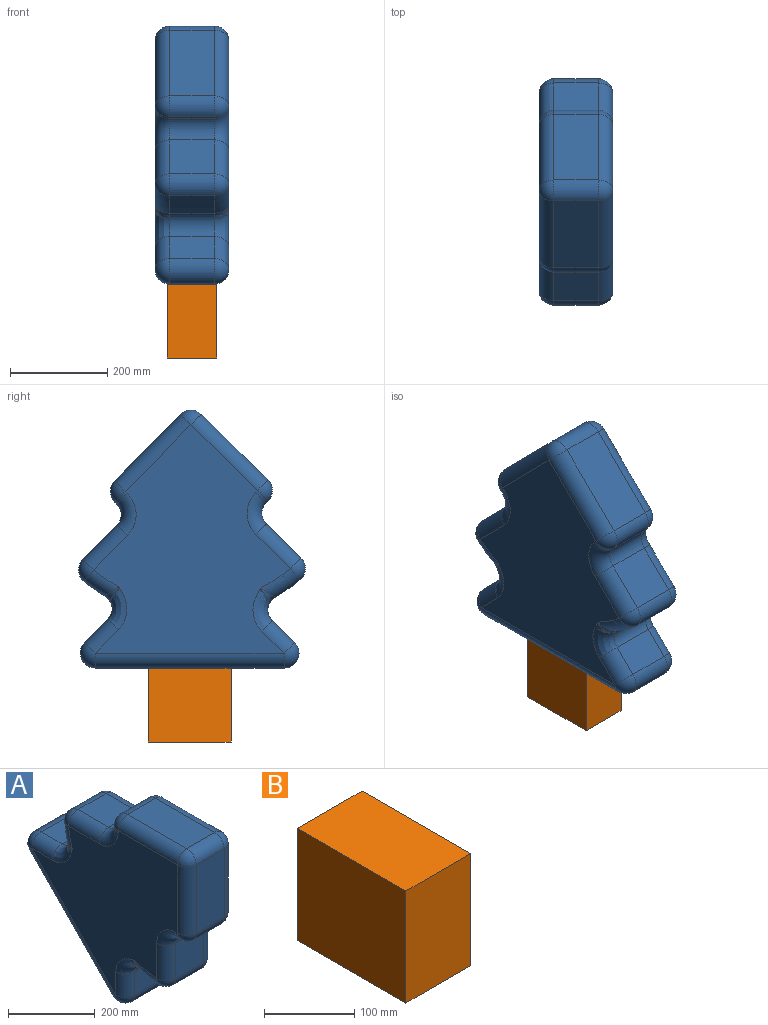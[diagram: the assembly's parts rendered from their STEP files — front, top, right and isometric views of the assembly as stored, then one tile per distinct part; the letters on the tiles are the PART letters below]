
ASSEMBLY  parts=2 mates=1
PART A: 72 faces, bbox 213.7x534.7x528.2 mm
  f0: cylinder r=349.59mm len=91.08mm, axis (-1,0,0), area 4696.8mm2, adj f2,f19,f20,f70
  f1: torus R=318.93mm, axis (1,0,0), area 3328.4mm2, adj f7,f11,f25,f53
  f2: torus R=318.93mm, axis (1,0,0), area 2790.6mm2, adj f0,f5,f26,f68
  f3: plane 99.76x91.08mm, normal (0,-1,0), area 9086.2mm2, adj f29,f30,f40,f41
  f4: plane 99.76x91.08mm, normal (0,0,1), area 9086.2mm2, adj f13,f14,f20,f21
  f5: plane 473.42x466.9mm, normal (-1,0,0), area 117312.5mm2, adj f2,f17,f21,f22,f31,f32,f41,f42
  f6: plane 192.68x91.08mm, normal (0,-1,0), area 17549mm2, adj f33,f34,f42,f43
  f7: plane 473.42x466.91mm, normal (1,0,0), area 117312.5mm2, adj f1,f12,f13,f15,f19,f24,f29,f34
  f8: plane 91.08x5.65mm, normal (0,1,0), area 514.6mm2, adj f14,f15,f22,f23
  f9: plane 192.68x91.08mm, normal (0,0,1), area 17549mm2, adj f23,f24,f32,f33
  f10: plane 91.08x5.65mm, normal (0,0,-1), area 514.6mm2, adj f35,f40,f43,f46
  f11: cylinder r=349.59mm len=91.08mm, axis (-1,0,0), area 5649mm2, adj f1,f30,f31,f51
  f12: torus R=61.32mm, axis (1,0,0), area 3162.4mm2, adj f7,f13,f14,f15
  f13: cylinder r=30.66mm len=99.76mm, axis (0,-1,0), area 4804.7mm2, adj f4,f7,f12,f16
  f14: cylinder r=30.66mm len=91.08mm, axis (1,0,0), area 4386.5mm2, adj f4,f8,f12,f17
  f15: cylinder r=30.66mm len=30.66mm, axis (0,0,-1), area 272.1mm2, adj f7,f8,f12,f18
  f16: sphere r=30.66mm, area 952.7mm2, adj f13,f19,f20
  f17: torus R=61.32mm, axis (1,0,0), area 3162.4mm2, adj f5,f14,f21,f22
  f18: sphere r=30.66mm, area 940.1mm2, adj f15,f23,f24
  f19: torus R=318.93mm, axis (1,0,0), area 2790.6mm2, adj f0,f7,f16,f71
  f20: cylinder r=30.66mm len=91.08mm, axis (-1,0,0), area 4655.4mm2, adj f0,f4,f16,f26
  f21: cylinder r=30.66mm len=99.76mm, axis (0,1,0), area 4804.7mm2, adj f4,f5,f17,f26
  f22: cylinder r=30.66mm len=30.66mm, axis (0,0,1), area 272.1mm2, adj f5,f8,f17,f27
  f23: cylinder r=30.66mm len=91.08mm, axis (1,0,0), area 4386.5mm2, adj f8,f9,f18,f27
  f24: cylinder r=30.66mm len=192.68mm, axis (0,-1,0), area 9279.7mm2, adj f7,f9,f18,f28
  f25: sphere r=30.66mm, area 1567.2mm2, adj f1,f29,f30
  f26: sphere r=30.66mm, area 2142.7mm2, adj f2,f20,f21
  f27: sphere r=30.66mm, area 2013.2mm2, adj f22,f23,f32
  f28: sphere r=30.66mm, area 1476.7mm2, adj f24,f33,f34
  f29: cylinder r=30.66mm len=99.76mm, axis (0,0,1), area 4804.7mm2, adj f3,f7,f25,f36
  f30: cylinder r=30.66mm len=91.08mm, axis (-1,0,0), area 4655.4mm2, adj f3,f11,f25,f37
  f31: torus R=318.93mm, axis (1,0,0), area 3328.4mm2, adj f5,f11,f37,f50
  f32: cylinder r=30.66mm len=192.68mm, axis (0,1,0), area 9279.7mm2, adj f5,f9,f27,f38
  f33: cylinder r=30.66mm len=91.08mm, axis (1,0,0), area 4386.5mm2, adj f6,f9,f28,f38
  f34: cylinder r=30.66mm len=192.68mm, axis (0,0,1), area 9279.7mm2, adj f6,f7,f28,f39
  f35: cylinder r=30.66mm len=30.66mm, axis (0,1,0), area 272.1mm2, adj f7,f10,f36,f39
  f36: torus R=61.32mm, axis (1,0,0), area 3162.4mm2, adj f7,f29,f35,f40
  f37: sphere r=30.66mm, area 1567.2mm2, adj f30,f31,f41
  f38: sphere r=30.66mm, area 1476.7mm2, adj f32,f33,f42
  f39: sphere r=30.66mm, area 1476.7mm2, adj f34,f35,f43
  f40: cylinder r=30.66mm len=91.08mm, axis (1,0,0), area 4386.5mm2, adj f3,f10,f36,f44
  f41: cylinder r=30.66mm len=99.76mm, axis (0,0,-1), area 4804.7mm2, adj f3,f5,f37,f44
  f42: cylinder r=30.66mm len=192.68mm, axis (0,0,-1), area 9279.7mm2, adj f5,f6,f38,f45
  f43: cylinder r=30.66mm len=91.08mm, axis (1,0,0), area 4386.5mm2, adj f6,f10,f39,f45
  f44: torus R=61.32mm, axis (1,0,0), area 3162.4mm2, adj f5,f40,f41,f46
  f45: sphere r=30.66mm, area 1476.7mm2, adj f42,f43,f46
  f46: cylinder r=30.66mm len=30.66mm, axis (0,-1,0), area 272.1mm2, adj f5,f10,f44,f45
  f47: plane 91.08x68.11mm, normal (0,0,1), area 6203.5mm2, adj f62,f64,f67,f68,f70,f71
  f48: plane 91.08x64.5mm, normal (0,-1,0), area 5874.9mm2, adj f50,f51,f53,f54,f57,f58
  f49: plane 277.49x273.01mm, normal (0,0.71,-0.7), area 35457.2mm2, adj f57,f59,f62,f63
  f50: bspline ~71.09x69.35mm, area 550.9mm2, adj f31,f48,f51,f52
  f51: cylinder r=30.66mm len=91.08mm, axis (-1,0,0), area 5150.4mm2, adj f11,f48,f50,f53
  f52: bspline ~71.08x61.32mm, area 2905.4mm2, adj f5,f50,f54
  f53: bspline ~71.09x69.35mm, area 550.9mm2, adj f1,f48,f51,f55
  f54: cylinder r=30.66mm len=64.5mm, axis (0,0,1), area 3106.1mm2, adj f5,f48,f52,f56
  f55: bspline ~71.08x61.32mm, area 2905.3mm2, adj f7,f53,f58
  f56: sphere r=30.66mm, area 2557.5mm2, adj f54,f57,f59
  f57: cylinder r=30.66mm len=91.08mm, axis (-1,0,0), area 6602.2mm2, adj f48,f49,f56,f60
  f58: cylinder r=30.66mm len=64.5mm, axis (0,0,-1), area 3106.1mm2, adj f7,f48,f55,f60
  f59: cylinder r=30.66mm len=298.99mm, axis (0,-0.7,-0.71), area 18746.5mm2, adj f5,f49,f56,f61
  f60: sphere r=30.66mm, area 2557.5mm2, adj f57,f58,f63
  f61: sphere r=30.66mm, area 2558.3mm2, adj f59,f62,f64
  f62: cylinder r=30.66mm len=91.08mm, axis (1,0,0), area 6556.8mm2, adj f47,f49,f61,f65
  f63: cylinder r=30.66mm len=298.99mm, axis (0,0.7,0.71), area 18746.5mm2, adj f7,f49,f60,f65
  f64: cylinder r=30.66mm len=68.11mm, axis (0,1,0), area 3279.8mm2, adj f5,f47,f61,f66
  f65: sphere r=30.66mm, area 2021.9mm2, adj f62,f63,f67
  f66: bspline ~70.47x61.32mm, area 2933.5mm2, adj f5,f64,f68
  f67: cylinder r=30.66mm len=68.11mm, axis (0,-1,0), area 3279.8mm2, adj f7,f47,f65,f69
  f68: bspline ~69.5x65.39mm, area 487.4mm2, adj f2,f47,f66,f70
  f69: bspline ~70.47x61.32mm, area 2933.5mm2, adj f7,f67,f71
  f70: cylinder r=30.66mm len=91.08mm, axis (-1,0,0), area 5066.9mm2, adj f0,f47,f68,f71
  f71: bspline ~69.5x65.39mm, area 487.4mm2, adj f19,f47,f69,f70
PART B: 6 faces, bbox 101.6x170.5x152.4 mm
  f0: plane 170.46x152.4mm, normal (-1,0,0), area 25978.4mm2, adj f1,f3,f4,f5
  f1: plane 152.4x101.6mm, normal (0,-1,0), area 15483.8mm2, adj f0,f2,f4,f5
  f2: plane 170.46x152.4mm, normal (1,0,0), area 25978.4mm2, adj f1,f3,f4,f5
  f3: plane 152.4x101.6mm, normal (0,1,0), area 15483.8mm2, adj f0,f2,f4,f5
  f4: plane 170.46x101.6mm, normal (0,0,1), area 17319mm2, adj f0,f1,f2,f3
  f5: plane 170.46x101.6mm, normal (0,0,-1), area 17319mm2, adj f0,f1,f2,f3
PLACE A rot(axis=(-1,0,0),45.5deg) t=(-8.23,8.87,353.3)mm
PLACE B t=(-1.34,138.57,-111.1)mm
MATE fastened A.f49 <-> B.f4  axis (0,0,-1) through (-8.19,138.64,41.3)mm
